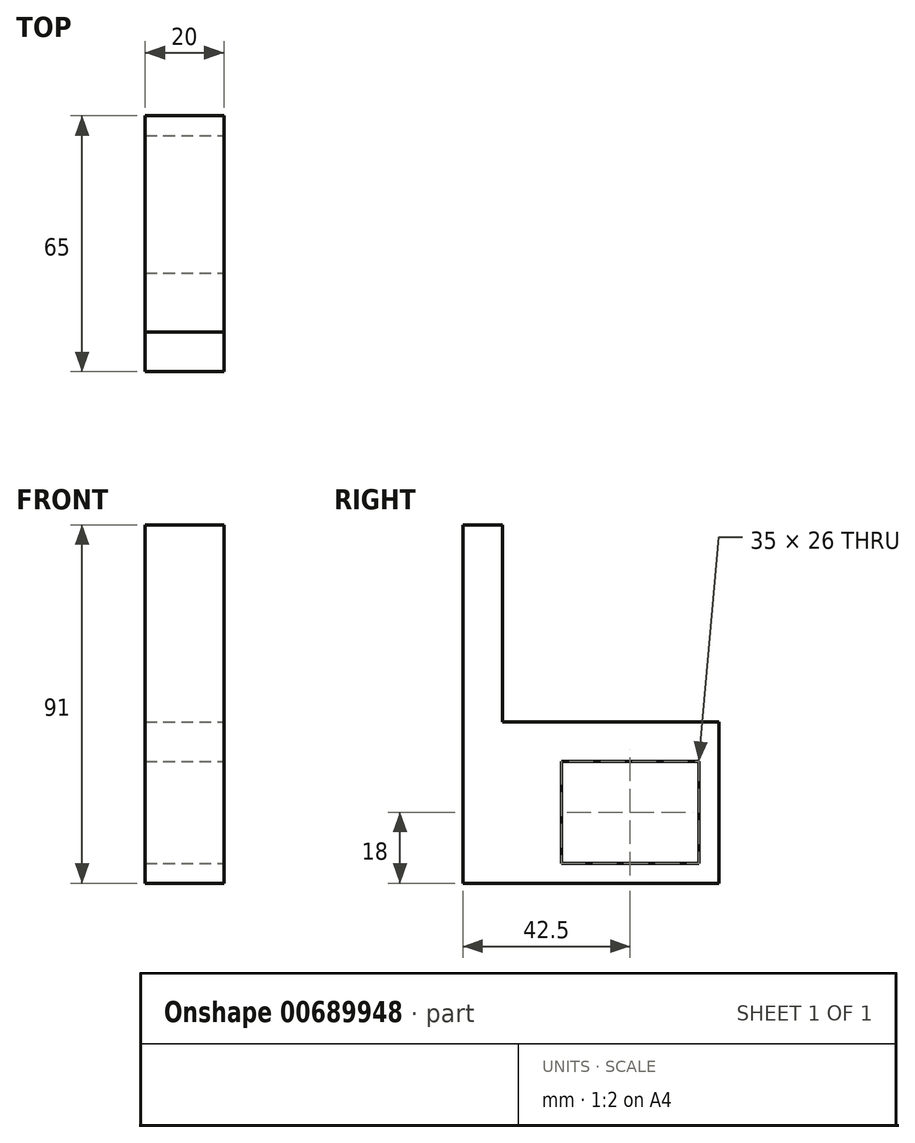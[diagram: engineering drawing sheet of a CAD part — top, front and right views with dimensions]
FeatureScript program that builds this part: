
annotation { "Feature Type Name" : "Feature", "Feature Type Description" : "" }
export const myFeature = defineFeature(function(context is Context, id is Id, definition is map)
    precondition{}
    {
        {
            var Q0;
            Q0=qCreatedBy(makeId("Right.planeOp"),FACE);
            var sketch = newSketch(context, id + "F0", { "sketchPlane" : qUnion([Q0])});
            skLineSegment(sketch, "E0.bottom", {"start": v(0, 0) * mm, "end": v(65, 0) * mm});
            skLineSegment(sketch, "E0.top", {"start": v(10, 41) * mm, "end": v(65, 41) * mm});
            skLineSegment(sketch, "E0.left", {"start": v(0, 0) * mm, "end": v(0, 41) * mm});
            skLineSegment(sketch, "E0.right", {"start": v(65, 0) * mm, "end": v(65, 41) * mm});
            skLineSegment(sketch, "E1.bottom", {"start": v(25, 31) * mm, "end": v(60, 31) * mm});
            skLineSegment(sketch, "E1.top", {"start": v(25, 5) * mm, "end": v(60, 5) * mm});
            skLineSegment(sketch, "E1.left", {"start": v(25, 31) * mm, "end": v(25, 5) * mm});
            skLineSegment(sketch, "E1.right", {"start": v(60, 31) * mm, "end": v(60, 5) * mm});
            skLineSegment(sketch, "E2", {"start": v(10, 41) * mm, "end": v(10, 91) * mm});
            skLineSegment(sketch, "E3", {"start": v(10, 91) * mm, "end": v(0, 91) * mm});
            skLineSegment(sketch, "E4", {"start": v(0, 91) * mm, "end": v(0, 41) * mm});
            skPoint(sketch, "E5", {"position": v(10, 41) * mm});
            skPoint(sketch, "E6", {"position": v(0, 41) * mm});
            skSolve(sketch);
        }
        {
            var Q0;
            Q0=makeQuery(id+"F0.imprint","IMPRINT",FACE,{"disambiguationData":[TD([[makeQuery(id+"F0.imprint","IMPRINT",EDGE,{"derivedFrom":sQuery(id+"F0.wireOp",EDGE,"E0.bottom")}),1.0]])]});
            extrude(context, id + "F1", {"entities" : qUnion([Q0]), "oppositeDirection" : true, "depth" : 20 * mm, "offsetDistance" : 25.4 * mm});
        }
        {
            var Q0;
            Q0=makeQuery(id+"F1.opExtrude","CAP_FACE",FACE,{"disambiguationData":[OSD([sQuery(id+"F0.wireOp",EDGE,"E0.bottom"),sQuery(id+"F0.wireOp",EDGE,"E0.top"),sQuery(id+"F0.wireOp",EDGE,"E0.left"),sQuery(id+"F0.wireOp",EDGE,"E0.right"),sQuery(id+"F0.wireOp",EDGE,"E1.bottom"),sQuery(id+"F0.wireOp",EDGE,"E1.top"),sQuery(id+"F0.wireOp",EDGE,"E1.left"),sQuery(id+"F0.wireOp",EDGE,"E1.right"),sQuery(id+"F0.wireOp",EDGE,"E2"),sQuery(id+"F0.wireOp",EDGE,"E3"),sQuery(id+"F0.wireOp",EDGE,"E4")])],"isStart":false});
            cPlane(context, id + "F2", {"entities" : qUnion([Q0]), "cplaneType" : CPlaneType.OFFSET, "offset" : 25.4 * mm, "width" : 152.4 * mm, "height" : 152.4 * mm});
        }
    });
